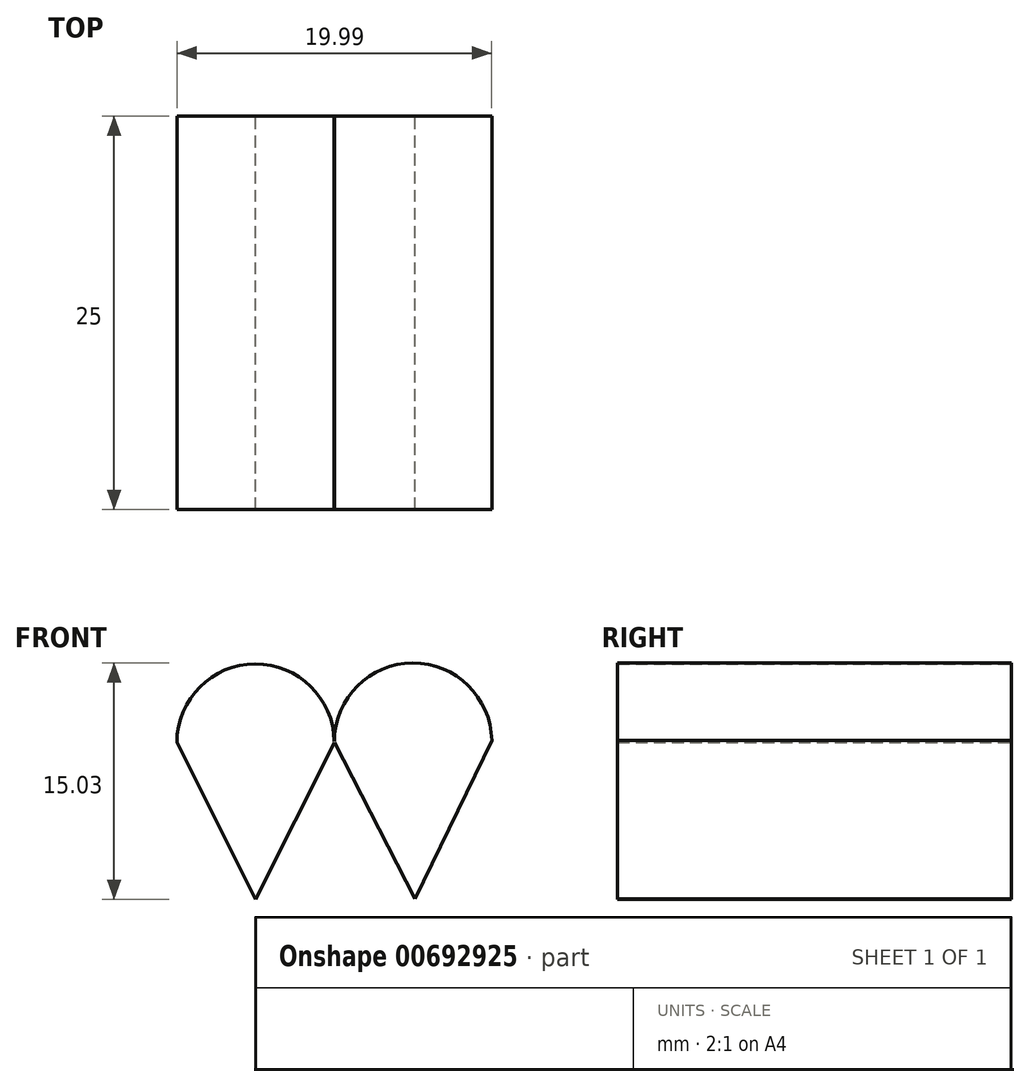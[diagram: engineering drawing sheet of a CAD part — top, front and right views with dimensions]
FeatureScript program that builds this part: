
annotation { "Feature Type Name" : "Feature", "Feature Type Description" : "" }
export const myFeature = defineFeature(function(context is Context, id is Id, definition is map)
    precondition{}
    {
        {
            var Q0;
            Q0=qCreatedBy(makeId("Front.planeOp"),FACE);
            var sketch = newSketch(context, id + "F0", { "sketchPlane" : qUnion([Q0])});
            skLineSegment(sketch, "E0", {"start": v(-52.25, 0) * mm, "end": v(-47.25, -10) * mm});
            skLineSegment(sketch, "E1", {"start": v(-47.25, -10) * mm, "end": v(-42.25, 0) * mm});
            skArc(sketch, "E2", {"start": v(-42.25, 0) * mm, "mid": v(-47.25, 4.97) * mm, "end": v(-52.25, 0) * mm});
            skLineSegment(sketch, "E3.MirrorCS", {"start": v(-32.26, 0.12) * mm, "end": v(-37.14, -9.94) * mm});
            skLineSegment(sketch, "E4.MirrorCS", {"start": v(-37.14, -9.94) * mm, "end": v(-42.25, 0) * mm});
            skArc(sketch, "E5.MirrorCS", {"start": v(-42.25, 0) * mm, "mid": v(-37.31, 5.03) * mm, "end": v(-32.26, 0.12) * mm});
            skLineSegment(sketch, "E6", {"start": v(-52.25, 0) * mm, "end": v(-32.26, 0.12) * mm});
            skLineSegment(sketch, "E7", {"start": v(-37.25, 0.03) * mm, "end": v(-37.14, -9.94) * mm});
            skLineSegment(sketch, "E8", {"start": v(-47.25, -0.03) * mm, "end": v(-47.25, -10) * mm});
            skSolve(sketch);
        }
        {
            var Q0;
            Q0 = qSketchRegion(id + "F0", true);
            extrude(context, id + "F1", {"entities" : qUnion([Q0]), "depth" : 25 * mm, "offsetDistance" : 25 * mm});
        }
    });
